# Revit family: NLRS_57_DUA_UN_plenum_for_supply_wall_grill_wto_LT_Solid_Air
name_source: partatom
category: Duct Accessories
units: mm (PartAtom-declared; Revit-internal decimal feet)

## family parameters
Always vertical = Yes
Cut with Voids When Loaded = No
Part Type = Attaches To
Round Connector Dimension = Use Diameter
Shared = No
Work Plane-Based = No

## types (1)
- WTOO
    Assembly Code = 57.00
    Default Elevation = 0 mm  [stored 0 ft]
    Description = WTO, plenum for wall grill
    Manufacturer = Solid Air Climate Solutions
    Model = WTO, plenum for wall grill
    NLRS_C_content_datum_gewijzigd = 02-12-2024
    NLRS_C_content_provider = Solid Air Climate Solutions
    NLRS_C_content_versie = 3.21.01
    NLRS_C_description = WTO, plenum for wall grill
    SACS_Data_Hidden = WTO
    SACS_Dummy = 1
    URL = https://solid-air.nl

note: [stored X ft] marks values corroborated as IEEE doubles in the binary element streams (Revit-internal decimal feet)

## geometry (parser evidence)
native form markers: Sweep x4
no freeform markers — native parametric forms only
